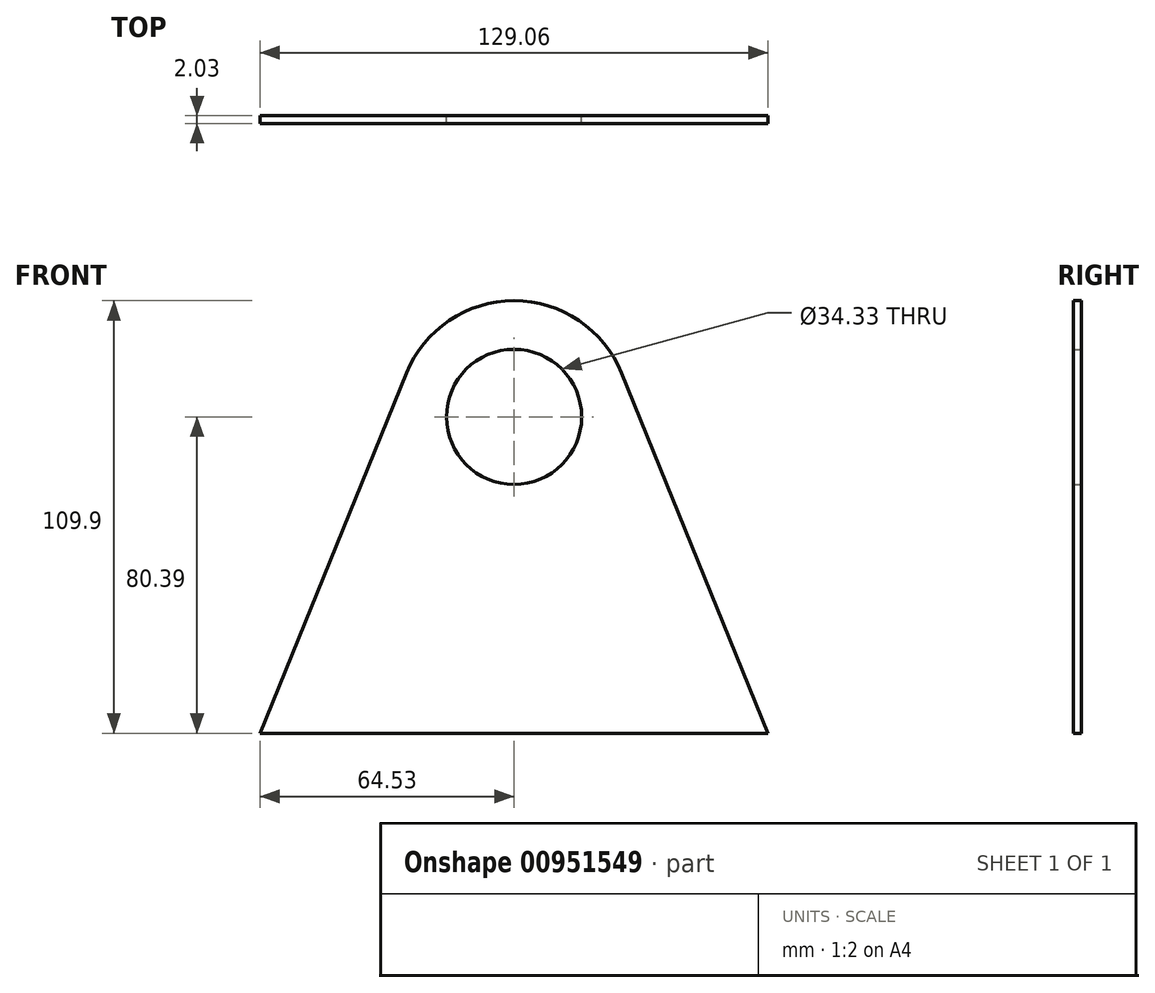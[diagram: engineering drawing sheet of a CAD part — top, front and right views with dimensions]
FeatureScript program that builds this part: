
annotation { "Feature Type Name" : "Feature", "Feature Type Description" : "" }
export const myFeature = defineFeature(function(context is Context, id is Id, definition is map)
    precondition{}
    {
        {
            var Q0;
            Q0=qCreatedBy(makeId("Front.planeOp"),FACE);
            var sketch = newSketch(context, id + "F0", { "sketchPlane" : qUnion([Q0])});
            skCircle(sketch, "E0", {"center": v(0, 0) * mm, "radius": 29.51 * mm});
            skLineSegment(sketch, "E1", {"start": v(-27.34, 11.11) * mm, "end": v(-64.53, -80.39) * mm});
            skLineSegment(sketch, "E2", {"start": v(-64.53, -80.39) * mm, "end": v(64.53, -80.39) * mm});
            skLineSegment(sketch, "E3", {"start": v(64.53, -80.39) * mm, "end": v(27.34, 11.11) * mm});
            skPoint(sketch, "E4", {"position": v(0, -80.39) * mm});
            skCircle(sketch, "E5", {"center": v(0, 0) * mm, "radius": 17.17 * mm});
            skSolve(sketch);
        }
        {
            var Q0;
            Q0 = qSketchRegion(id + "F0", true);
            extrude(context, id + "F1", {"entities" : qUnion([Q0]), "depth" : 2.03 * mm, "offsetDistance" : 25.4 * mm});
        }
    });
